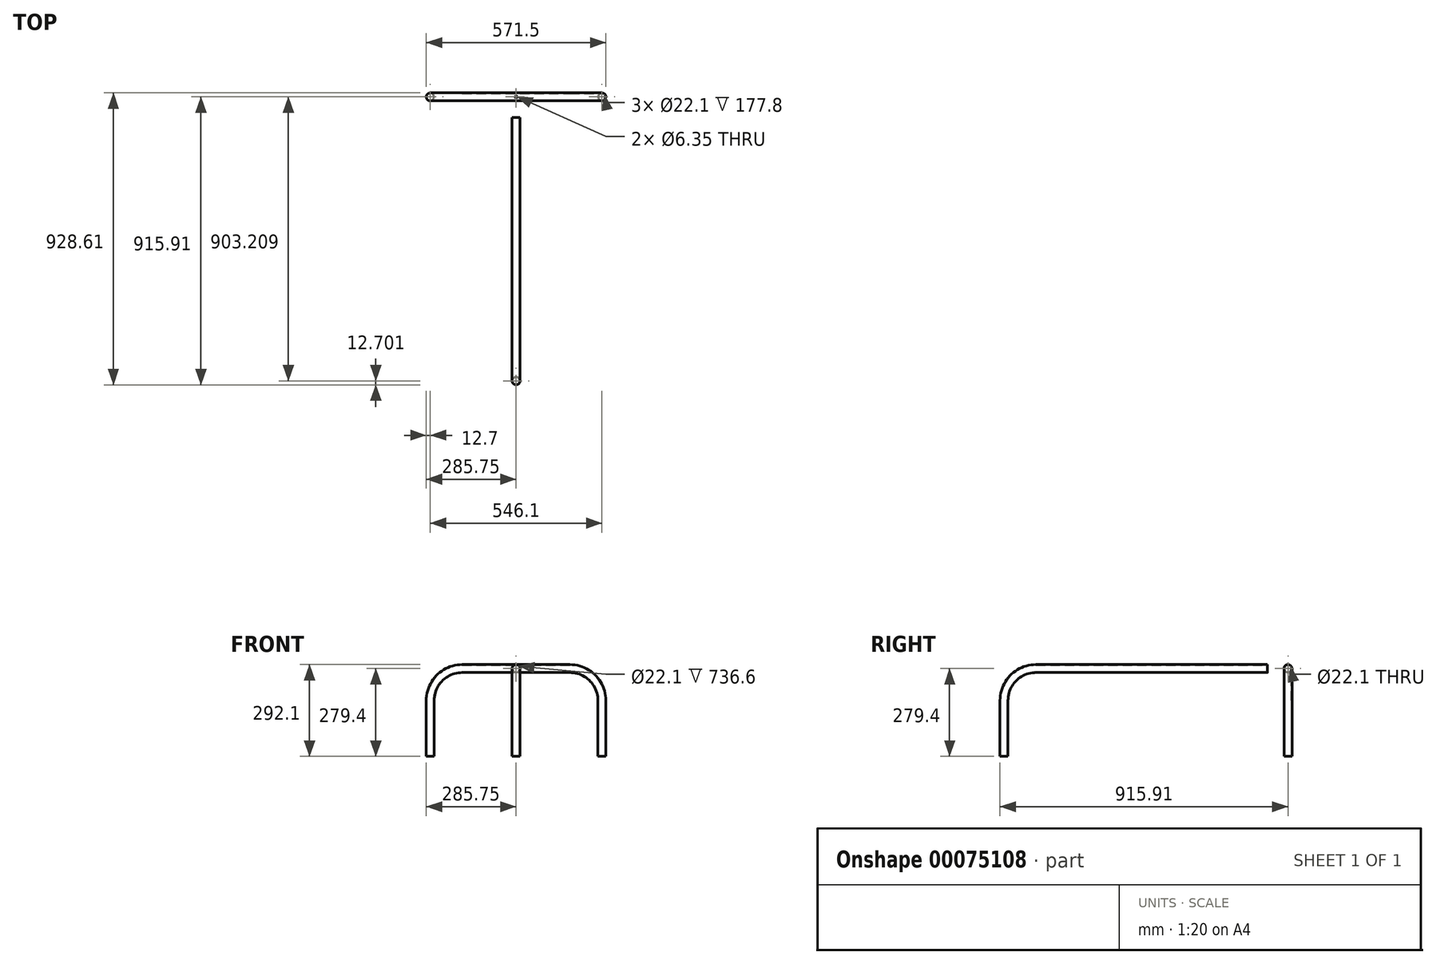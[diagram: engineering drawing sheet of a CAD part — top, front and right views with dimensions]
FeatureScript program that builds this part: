
annotation { "Feature Type Name" : "Feature", "Feature Type Description" : "" }
export const myFeature = defineFeature(function(context is Context, id is Id, definition is map)
    precondition{}
    {
        {
            var Q0;
            Q0=qCreatedBy(makeId("Front.planeOp"),FACE);
            var sketch = newSketch(context, id + "F0", { "sketchPlane" : qUnion([Q0])});
            skLineSegment(sketch, "E0", {"start": v(-273.05, 0) * mm, "end": v(-273.05, 177.8) * mm});
            skLineSegment(sketch, "E1", {"start": v(-171.45, 279.4) * mm, "end": v(171.45, 279.4) * mm});
            skLineSegment(sketch, "E2", {"start": v(273.05, 177.8) * mm, "end": v(273.05, 0) * mm});
            skArc(sketch, "E3", {"start": v(-171.45, 279.4) * mm, "mid": v(-243.3, 249.64) * mm, "end": v(-273.05, 177.8) * mm});
            skArc(sketch, "E4", {"start": v(273.05, 177.8) * mm, "mid": v(243.3, 249.64) * mm, "end": v(171.45, 279.4) * mm});
            skLineSegment(sketch, "E5", {"start": v(0, 0) * mm, "end": v(0, 35.13) * mm, "construction": true});
            skSolve(sketch);
        }
        {
            var Q0;
            Q0=qCreatedBy(makeId("Top.planeOp"),FACE);
            var sketch = newSketch(context, id + "F1", { "sketchPlane" : qUnion([Q0])});
            skPoint(sketch, "E6.0", {"position": v(-273.05, 0) * mm});
            skCircle(sketch, "E7", {"center": v(-273.05, 0) * mm, "radius": 12.7 * mm});
            skCircle(sketch, "E8", {"center": v(-273.05, 0) * mm, "radius": 11.05 * mm});
            skSolve(sketch);
        }
        {
            var Q0;
            Q0=makeQuery(id+"F1.imprint","IMPRINT",FACE,{"disambiguationData":[TD([[makeQuery(id+"F1.imprint","IMPRINT",EDGE,{"derivedFrom":sQuery(id+"F1.wireOp",EDGE,"E7")}),1.0]])]});
            var Q1;
            Q1=sQuery(id+"F0.wireOp",EDGE,"E3");
            var Q2;
            Q2=sQuery(id+"F0.wireOp",EDGE,"E0");
            var Q3;
            Q3=sQuery(id+"F0.wireOp",EDGE,"E3");
            var Q4;
            Q4=sQuery(id+"F0.wireOp",EDGE,"E1");
            var Q5;
            Q5=sQuery(id+"F0.wireOp",EDGE,"E4");
            var Q6;
            Q6=sQuery(id+"F0.wireOp",EDGE,"E2");
            sweep(context, id + "F2", {"profiles" : qUnion([Q0]), "surfaceProfiles" : qUnion([Q1]), "path" : qUnion([Q2, Q3, Q4, Q5, Q6])});
        }
        {
            var Q0;
            Q0=qCreatedBy(makeId("Right.planeOp"),FACE);
            var sketch = newSketch(context, id + "F3", { "sketchPlane" : qUnion([Q0])});
            skLineSegment(sketch, "E9", {"start": v(-65, 279.4) * mm, "end": v(-801.6, 279.4) * mm});
            skLineSegment(sketch, "E10", {"start": v(-903.2, 177.8) * mm, "end": v(-903.2, 0) * mm});
            skArc(sketch, "E11", {"start": v(-801.6, 279.4) * mm, "mid": v(-873.45, 249.64) * mm, "end": v(-903.2, 177.8) * mm});
            skSolve(sketch);
        }
        {
            var Q0;
            Q0=qCreatedBy(makeId("Top.planeOp"),FACE);
            var sketch = newSketch(context, id + "F4", { "sketchPlane" : qUnion([Q0])});
            skCircle(sketch, "E12", {"center": v(0, -903.2) * mm, "radius": 12.7 * mm});
            skCircle(sketch, "E13", {"center": v(0, -903.2) * mm, "radius": 11.05 * mm});
            skSolve(sketch);
        }
        {
            var Q0;
            Q0=makeQuery(id+"F4.imprint","IMPRINT",FACE,{"disambiguationData":[TD([[makeQuery(id+"F4.imprint","IMPRINT",EDGE,{"derivedFrom":sQuery(id+"F4.wireOp",EDGE,"E12")}),1.0]])]});
            var Q1;
            Q1=sQuery(id+"F3.wireOp",EDGE,"E10");
            var Q2;
            Q2=sQuery(id+"F3.wireOp",EDGE,"E11");
            var Q3;
            Q3=sQuery(id+"F3.wireOp",EDGE,"E9");
            sweep(context, id + "F5", {"profiles" : qUnion([Q0]), "path" : qUnion([Q1, Q2, Q3])});
        }
        {
            var Q0;
            Q0=sQuery(id+"F0.wireOp",VERTEX,"E3.start");
            var Q1;
            Q1=sQuery(id+"F0.wireOp",VERTEX,"E4.end");
            var Q2;
            Q2=sQuery(id+"F3.wireOp",VERTEX,"E9.start");
            cPlane(context, id + "F6", {"entities" : qUnion([Q0, Q1, Q2]), "cplaneType" : CPlaneType.THREE_POINT, "offset" : 152.4 * mm, "width" : 152.4 * mm, "height" : 152.4 * mm});
        }
        {
            var Q0;
            Q0=qCreatedBy(id+"F6.planeOp",FACE);
            cPlane(context, id + "F7", {"entities" : qUnion([Q0]), "cplaneType" : CPlaneType.OFFSET, "offset" : 12.7 * mm, "width" : 152.4 * mm, "height" : 152.4 * mm});
        }
        {
            var Q0;
            Q0=qCreatedBy(id+"F7.planeOp",FACE);
            var sketch = newSketch(context, id + "F8", { "sketchPlane" : qUnion([Q0])});
            skLineSegment(sketch, "E14.0", {"start": v(-171.45, 0) * mm, "end": v(171.45, 0) * mm, "construction": true});
            skPoint(sketch, "E15", {"position": v(0, 0) * mm});
            skSolve(sketch);
        }
        {
            var Q0;
            Q0=sQuery(id+"F8.wireOp",VERTEX,"E15");
            var Q1;
            Q1=makeQuery(id+"F2.opSweep","SWEPT_BODY",BODY,{"disambiguationData":[OSD([sQuery(id+"F0.wireOp",EDGE,"E2"),sQuery(id+"F1.wireOp",EDGE,"E7"),sQuery(id+"F1.wireOp",EDGE,"E8")])]});
            hole(context, id + "F9", {"style" : HoleStyle.SIMPLE, "endStyle" : HoleEndStyle.THROUGH, "holeDiameter" : 6.35 * mm, "locations" : qUnion([Q0]), "scope" : qUnion([Q1]), "isTappedThrough" : true});
        }
    });
